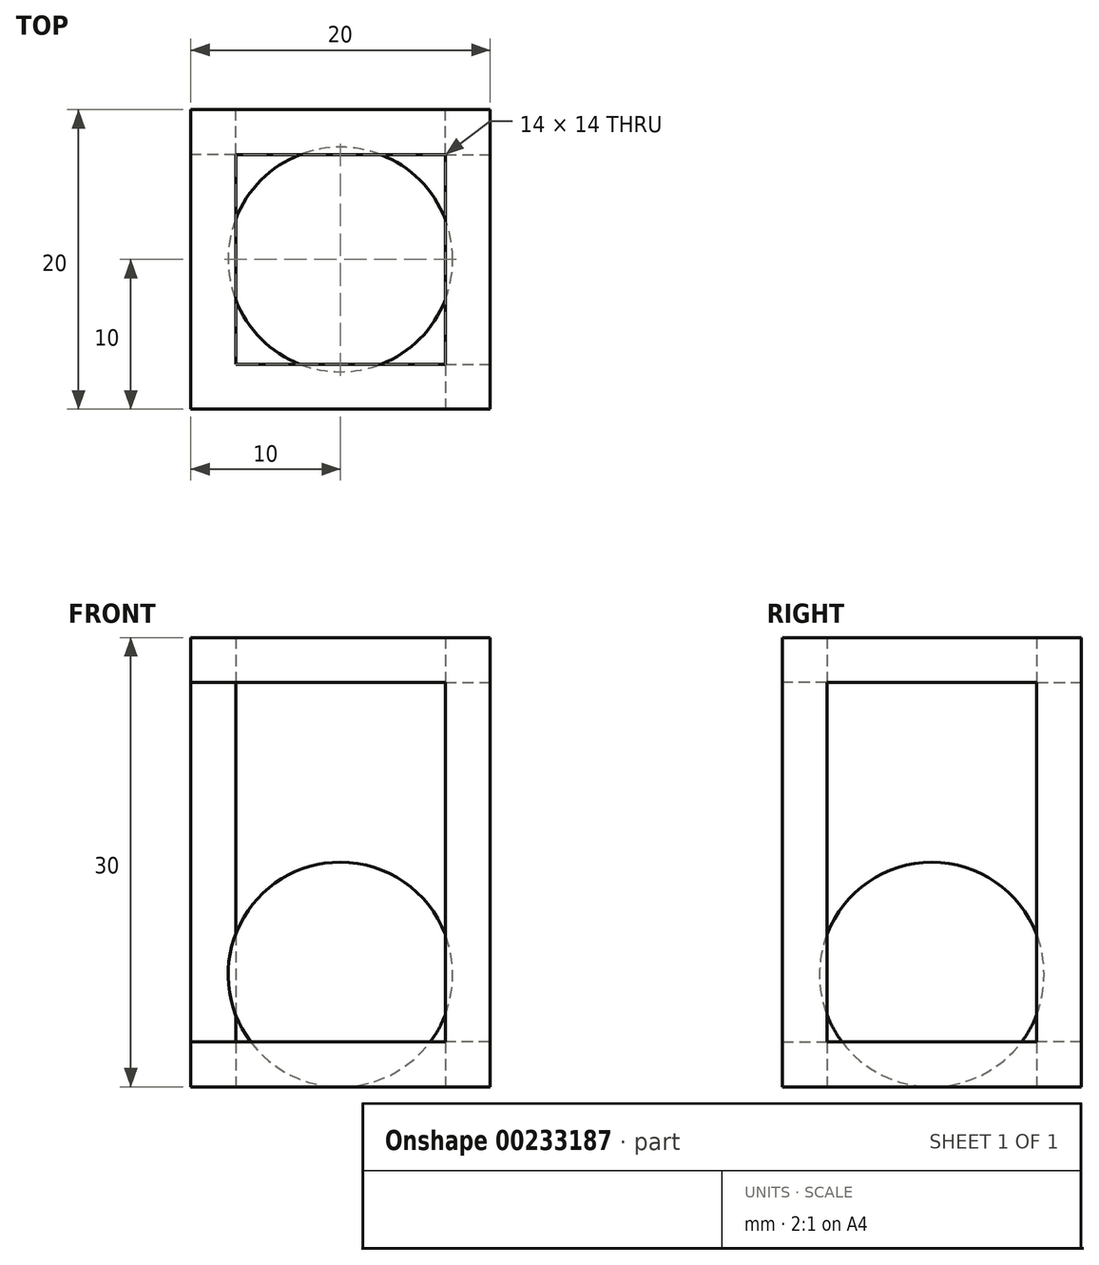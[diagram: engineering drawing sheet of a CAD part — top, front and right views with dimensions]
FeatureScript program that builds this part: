
annotation { "Feature Type Name" : "Feature", "Feature Type Description" : "" }
export const myFeature = defineFeature(function(context is Context, id is Id, definition is map)
    precondition{}
    {
        {
            var Q0;
            Q0=qCreatedBy(makeId("Top.planeOp"),FACE);
            var sketch = newSketch(context, id + "F0", { "sketchPlane" : qUnion([Q0])});
            skLineSegment(sketch, "E0.bottom", {"start": v(10, 10) * mm, "end": v(-10, 10) * mm});
            skLineSegment(sketch, "E0.top", {"start": v(10, -10) * mm, "end": v(-10, -10) * mm});
            skLineSegment(sketch, "E0.left", {"start": v(10, 10) * mm, "end": v(10, -10) * mm});
            skLineSegment(sketch, "E0.right", {"start": v(-10, 10) * mm, "end": v(-10, -10) * mm});
            skPoint(sketch, "E0.middle", {"position": v(0, 0) * mm});
            skLineSegment(sketch, "E1.bottom", {"start": v(-7, 7) * mm, "end": v(7, 7) * mm});
            skLineSegment(sketch, "E1.top", {"start": v(-7, -7) * mm, "end": v(7, -7) * mm});
            skLineSegment(sketch, "E1.left", {"start": v(-7, 7) * mm, "end": v(-7, -7) * mm});
            skLineSegment(sketch, "E1.right", {"start": v(7, 7) * mm, "end": v(7, -7) * mm});
            skLineSegment(sketch, "E2.bottom", {"start": v(-7, 7) * mm, "end": v(-10, 7) * mm});
            skLineSegment(sketch, "E2.top", {"start": v(-7, 10) * mm, "end": v(-10, 10) * mm});
            skLineSegment(sketch, "E2.left", {"start": v(-7, 7) * mm, "end": v(-7, 10) * mm});
            skLineSegment(sketch, "E2.right", {"start": v(-10, 7) * mm, "end": v(-10, 10) * mm});
            skLineSegment(sketch, "E3.bottom", {"start": v(7, 7) * mm, "end": v(10, 7) * mm});
            skLineSegment(sketch, "E3.top", {"start": v(7, 10) * mm, "end": v(10, 10) * mm});
            skLineSegment(sketch, "E3.left", {"start": v(7, 7) * mm, "end": v(7, 10) * mm});
            skLineSegment(sketch, "E3.right", {"start": v(10, 7) * mm, "end": v(10, 10) * mm});
            skLineSegment(sketch, "E4.bottom", {"start": v(7, -7) * mm, "end": v(10, -7) * mm});
            skLineSegment(sketch, "E4.top", {"start": v(7, -10) * mm, "end": v(10, -10) * mm});
            skLineSegment(sketch, "E4.left", {"start": v(7, -7) * mm, "end": v(7, -10) * mm});
            skLineSegment(sketch, "E4.right", {"start": v(10, -7) * mm, "end": v(10, -10) * mm});
            skLineSegment(sketch, "E5.bottom", {"start": v(-10, -10) * mm, "end": v(-7, -10) * mm});
            skLineSegment(sketch, "E5.top", {"start": v(-10, -7) * mm, "end": v(-7, -7) * mm});
            skLineSegment(sketch, "E5.left", {"start": v(-10, -10) * mm, "end": v(-10, -7) * mm});
            skLineSegment(sketch, "E5.right", {"start": v(-7, -10) * mm, "end": v(-7, -7) * mm});
            skSolve(sketch);
        }
        {
            var Q0;
            Q0=makeQuery(id+"F0.imprint","IMPRINT",FACE,{"disambiguationData":[TD([[makeQuery(id+"F0.imprint","IMPRINT",EDGE,{"derivedFrom":sQuery(id+"F0.wireOp",EDGE,"E0.top")}),-1.0]])]});
            var Q1;
            Q1=makeQuery(id+"F0.imprint","IMPRINT",FACE,{"disambiguationData":[TD([[makeQuery(id+"F0.imprint","IMPRINT",EDGE,{"derivedFrom":sQuery(id+"F0.wireOp",EDGE,"E0.right")}),1.0]])]});
            var Q2;
            Q2=makeQuery(id+"F0.imprint","IMPRINT",FACE,{"disambiguationData":[TD([[makeQuery(id+"F0.imprint","IMPRINT",EDGE,{"derivedFrom":sQuery(id+"F0.wireOp",EDGE,"E0.bottom")}),1.0]])]});
            var Q3;
            Q3=makeQuery(id+"F0.imprint","IMPRINT",FACE,{"disambiguationData":[TD([[makeQuery(id+"F0.imprint","IMPRINT",EDGE,{"derivedFrom":sQuery(id+"F0.wireOp",EDGE,"E0.left")}),-1.0]])]});
            var Q4;
            Q4=makeQuery(id+"F0.imprint","IMPRINT",FACE,{"disambiguationData":[TD([[makeQuery(id+"F0.imprint","IMPRINT",EDGE,{"derivedFrom":sQuery(id+"F0.wireOp",EDGE,"E5.bottom")}),1.0]])]});
            var Q5;
            Q5=makeQuery(id+"F0.imprint","IMPRINT",FACE,{"disambiguationData":[TD([[makeQuery(id+"F0.imprint","IMPRINT",EDGE,{"derivedFrom":sQuery(id+"F0.wireOp",EDGE,"E4.bottom")}),-1.0]])]});
            var Q6;
            Q6=makeQuery(id+"F0.imprint","IMPRINT",FACE,{"disambiguationData":[TD([[makeQuery(id+"F0.imprint","IMPRINT",EDGE,{"derivedFrom":sQuery(id+"F0.wireOp",EDGE,"E3.bottom")}),1.0]])]});
            var Q7;
            Q7=makeQuery(id+"F0.imprint","IMPRINT",FACE,{"disambiguationData":[TD([[makeQuery(id+"F0.imprint","IMPRINT",EDGE,{"derivedFrom":sQuery(id+"F0.wireOp",EDGE,"E2.bottom")}),-1.0]])]});
            extrude(context, id + "F1", {"entities" : qUnion([Q0, Q1, Q2, Q3, Q4, Q5, Q6, Q7]), "depth" : 3 * mm});
        }
        {
            var Q0;
            Q0=makeQuery(id+"F0.imprint","IMPRINT",FACE,{"disambiguationData":[TD([[makeQuery(id+"F0.imprint","IMPRINT",EDGE,{"derivedFrom":sQuery(id+"F0.wireOp",EDGE,"E5.bottom")}),1.0]])]});
            var Q1;
            Q1=makeQuery(id+"F0.imprint","IMPRINT",FACE,{"disambiguationData":[TD([[makeQuery(id+"F0.imprint","IMPRINT",EDGE,{"derivedFrom":sQuery(id+"F0.wireOp",EDGE,"E2.bottom")}),-1.0]])]});
            var Q2;
            Q2=makeQuery(id+"F0.imprint","IMPRINT",FACE,{"disambiguationData":[TD([[makeQuery(id+"F0.imprint","IMPRINT",EDGE,{"derivedFrom":sQuery(id+"F0.wireOp",EDGE,"E3.bottom")}),1.0]])]});
            var Q3;
            Q3=makeQuery(id+"F0.imprint","IMPRINT",FACE,{"disambiguationData":[TD([[makeQuery(id+"F0.imprint","IMPRINT",EDGE,{"derivedFrom":sQuery(id+"F0.wireOp",EDGE,"E4.bottom")}),-1.0]])]});
            extrude(context, id + "F2", {"entities" : qUnion([Q0, Q1, Q2, Q3]), "operationType" : NewBodyOperationType.ADD, "depth" : 30 * mm});
        }
        {
            var Q0;
            Q0 = qSketchRegion(id + "F0", true);
            extrude(context, id + "F3", {"entities" : qUnion([Q0]), "operationType" : NewBodyOperationType.ADD, "depth" : 30 * mm, "hasSecondDirection" : true, "secondDirectionOppositeDirection" : false, "secondDirectionDepth" : 27 * mm});
        }
        {
            var Q0;
            Q0=qCreatedBy(makeId("Front.planeOp"),FACE);
            var sketch = newSketch(context, id + "F4", { "sketchPlane" : qUnion([Q0])});
            skCircle(sketch, "E6", {"center": v(0, 7.5) * mm, "radius": 7.5 * mm});
            skLineSegment(sketch, "E7", {"start": v(0, 22.96) * mm, "end": v(0, 6.07) * mm, "construction": true});
            skLineSegment(sketch, "E8", {"start": v(0, 15) * mm, "end": v(0, 0) * mm});
            skSolve(sketch);
        }
        {
            var Q0;
            {var subQ0=sQuery(id+"F4.wireOp",EDGE,"E8");Q0=makeQuery(id+"F4.imprint","IMPRINT",FACE,{"disambiguationData":[TD([[makeQuery(id+"F4.imprint","IMPRINT",EDGE,{"derivedFrom":subQ0}),-1.0]])]});}
            var Q1;
            Q1=sQuery(id+"F4.wireOp",EDGE,"E8");
            revolve(context, id + "F5", {"entities" : qUnion([Q0]), "axis" : qUnion([Q1]), "revolveType" : RevolveType.FULL});
        }
    });
